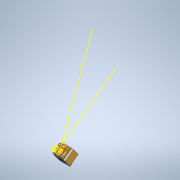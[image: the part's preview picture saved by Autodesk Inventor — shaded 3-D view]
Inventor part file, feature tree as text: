
AUTODESK INVENTOR PART (.ipt)
format: ipt  version: 2020 (Build 240168000, 168)  size: 366,592 bytes
history: native  units: mm
features: sketch x7, other x3, extrude x3, projected_geometry x2
ambient origin geometry x8: Origin, YZ Plane, XZ Plane, XY Plane, X Axis, Y Axis, Z Axis, Center Point
bodies: Solid1 (feature_tree)
feature tree (15):
  other  "nano cam assem.iam"
  other  "V1 session mount.ipt:1"
  other  "45 deg predator nano mount.ipt:1"
  extrude  "Extrusion1"  TaperAngle=0.0deg  [1 undecoded]
  extrude  "Extrusion2"  Depth=1.0mm TaperAngle=0.0deg
  extrude  "Extrusion3"  [1 undecoded]
  sketch  "Sketch1"  dims[d0=10.0mm d1=0.0mm d2=0.0mm]
  sketch  "Sketch1_1"  dims[d3=0.5mm d4=1.0mm d5=0.0mm]
  sketch  "Sketch6"
  sketch  "Sketch11"
  sketch  "Sketch5"  dims[d6=1.0mm d7=0.0mm]
  sketch  "Sketch7"
  projected_geometry  "Projected Loop1"
  sketch  "Sketch8"
  projected_geometry  "Projected Loop2"
note: 2 required parameter values undecoded (feature->parameter linkage not recoverable at this tier; creation-order binding heuristic only, values carry confidence <= 0.55)
